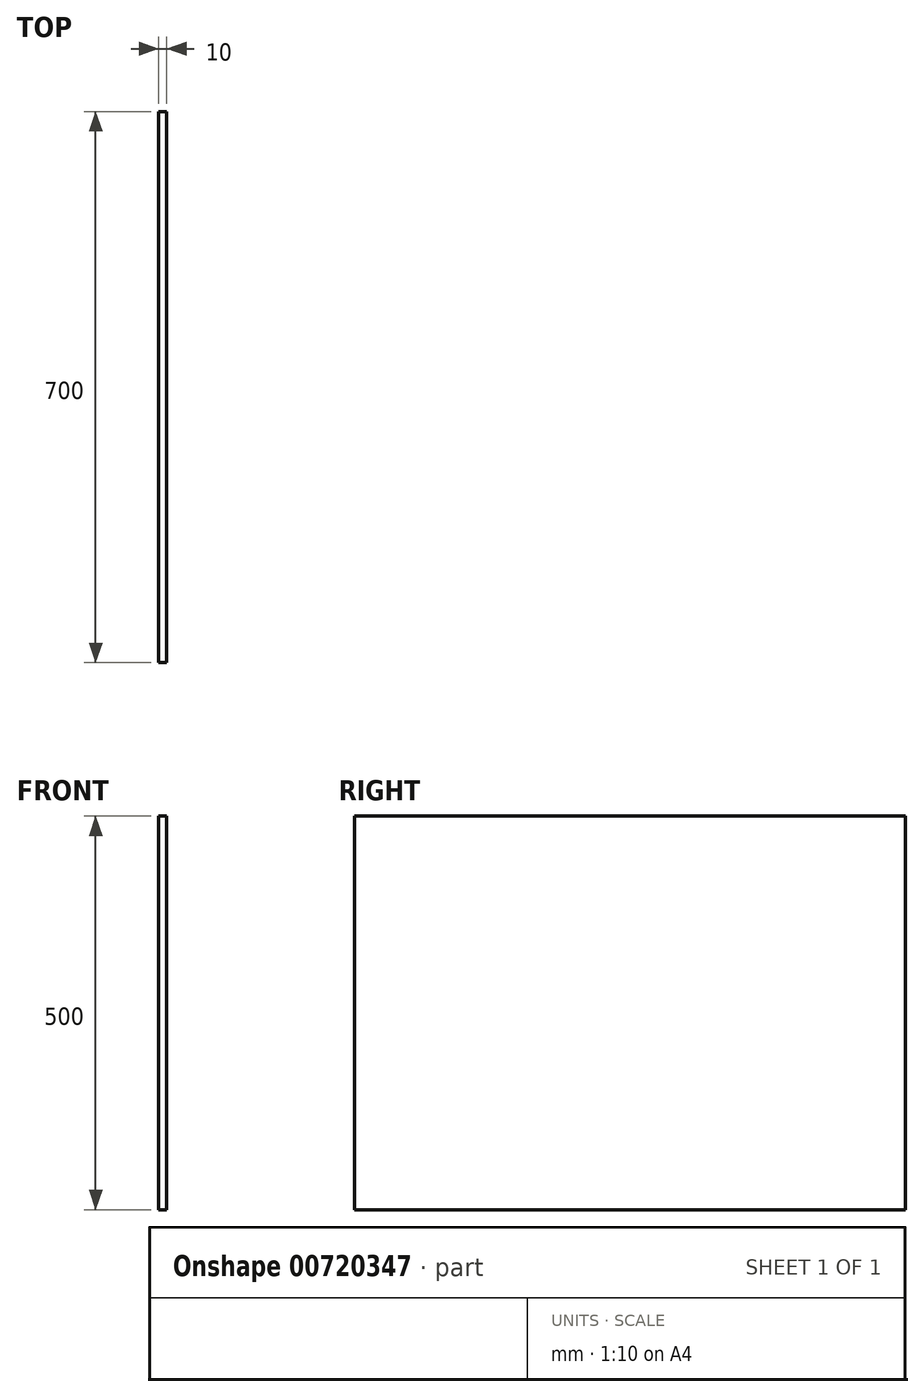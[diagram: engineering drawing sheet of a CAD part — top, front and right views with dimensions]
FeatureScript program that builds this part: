
annotation { "Feature Type Name" : "Feature", "Feature Type Description" : "" }
export const myFeature = defineFeature(function(context is Context, id is Id, definition is map)
    precondition{}
    {
        {
            var Q0;
            Q0=qCreatedBy(makeId("Front.planeOp"),FACE);
            var sketch = newSketch(context, id + "F0", { "sketchPlane" : qUnion([Q0])});
            skLineSegment(sketch, "E0.bottom", {"start": v(0, 0) * mm, "end": v(-10, 0) * mm});
            skLineSegment(sketch, "E0.top", {"start": v(0, -500) * mm, "end": v(-10, -500) * mm});
            skLineSegment(sketch, "E0.left", {"start": v(0, 0) * mm, "end": v(0, -500) * mm});
            skLineSegment(sketch, "E0.right", {"start": v(-10, 0) * mm, "end": v(-10, -500) * mm});
            skSolve(sketch);
        }
        {
            var Q0;
            Q0 = qSketchRegion(id + "F0", true);
            extrude(context, id + "F1", {"entities" : qUnion([Q0]), "depth" : 700 * mm, "offsetDistance" : 25 * mm});
        }
    });
